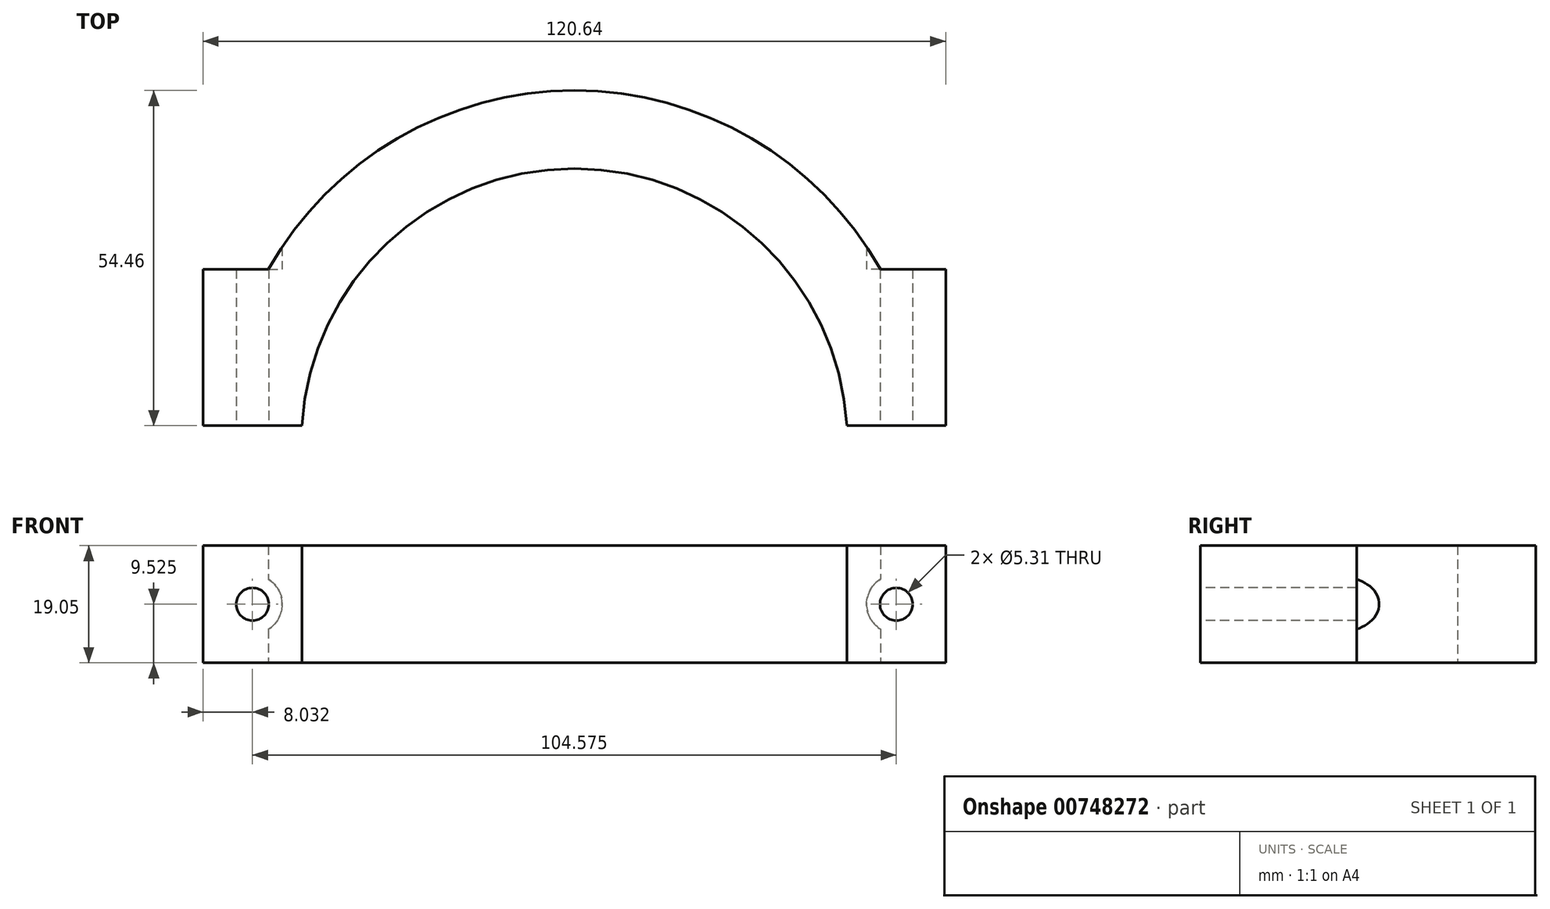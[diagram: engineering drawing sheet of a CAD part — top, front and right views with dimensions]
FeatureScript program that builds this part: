
annotation { "Feature Type Name" : "Feature", "Feature Type Description" : "" }
export const myFeature = defineFeature(function(context is Context, id is Id, definition is map)
    precondition{}
    {
        {
            var Q0;
            Q0=qCreatedBy(makeId("Top.planeOp"),FACE);
            var sketch = newSketch(context, id + "F0", { "sketchPlane" : qUnion([Q0])});
            skPoint(sketch, "E0.middle", {"position": v(0, 24.5) * mm});
            skArc(sketch, "E1", {"start": v(44.25, 27.05) * mm, "mid": v(0, 68.81) * mm, "end": v(-44.25, 27.05) * mm});
            skLineSegment(sketch, "E2", {"start": v(44.25, 27.05) * mm, "end": v(60.33, 27.05) * mm});
            skLineSegment(sketch, "E3", {"start": v(60.33, 27.05) * mm, "end": v(60.33, 52.45) * mm});
            skLineSegment(sketch, "E4", {"start": v(-60.33, 27.05) * mm, "end": v(-60.32, 52.45) * mm});
            skArc(sketch, "E5.0", {"start": v(49.7, 52.45) * mm, "mid": v(0, 81.51) * mm, "end": v(-49.7, 52.45) * mm});
            skLineSegment(sketch, "E6", {"start": v(-60.32, 52.45) * mm, "end": v(-49.7, 52.45) * mm});
            skLineSegment(sketch, "E7", {"start": v(60.33, 52.45) * mm, "end": v(49.7, 52.45) * mm});
            skLineSegment(sketch, "E8", {"start": v(-60.33, 27.05) * mm, "end": v(-44.25, 27.05) * mm});
            skSolve(sketch);
        }
        {
            var Q0;
            Q0 = qSketchRegion(id + "F0", true);
            extrude(context, id + "F1", {"entities" : qUnion([Q0]), "depth" : 19.05 * mm, "offsetDistance" : 25.4 * mm});
        }
        {
            var Q0;
            Q0=makeQuery(id+"F1.opExtrude","SWEPT_FACE",FACE,{"disambiguationData":[OSD([sQuery(id+"F0.wireOp",EDGE,"E8")])]});
            var sketch = newSketch(context, id + "F2", { "sketchPlane" : qUnion([Q0])});
            skLineSegment(sketch, "E9", {"start": v(-52.29, 19.05) * mm, "end": v(-52.29, 0) * mm, "construction": true});
            skLineSegment(sketch, "E10.0", {"start": v(-52.29, 9.53) * mm, "end": v(52.29, 9.53) * mm, "construction": true});
            skCircle(sketch, "E11", {"center": v(-52.29, 9.53) * mm, "radius": 2.65 * mm});
            skCircle(sketch, "E12", {"center": v(52.29, 9.53) * mm, "radius": 2.65 * mm});
            skSolve(sketch);
        }
        {
            var Q0;
            Q0 = qSketchRegion(id + "F2", true);
            extrude(context, id + "F3", {"entities" : qUnion([Q0]), "operationType" : NewBodyOperationType.REMOVE, "endBound" : BoundingType.THROUGH_ALL, "oppositeDirection" : true, "depth" : 25.4 * mm, "offsetDistance" : 25.4 * mm});
        }
        {
            var Q0;
            Q0=makeQuery(id+"F1.opExtrude","SWEPT_FACE",FACE,{"disambiguationData":[OSD([sQuery(id+"F0.wireOp",EDGE,"E7")])]});
            var sketch = newSketch(context, id + "F4", { "sketchPlane" : qUnion([Q0])});
            skLineSegment(sketch, "E13", {"start": v(-52.29, 9.53) * mm, "end": v(52.29, 9.53) * mm, "construction": true});
            skCircle(sketch, "E14", {"center": v(-52.29, 9.53) * mm, "radius": 4.83 * mm});
            skCircle(sketch, "E15", {"center": v(52.29, 9.53) * mm, "radius": 4.83 * mm});
            skLineSegment(sketch, "E16.0", {"start": v(-52.29, 79.38) * mm, "end": v(52.29, 79.38) * mm, "construction": true});
            skCircle(sketch, "E17", {"center": v(-52.29, 79.38) * mm, "radius": 4.83 * mm});
            skCircle(sketch, "E18", {"center": v(52.29, 79.38) * mm, "radius": 4.83 * mm});
            skSolve(sketch);
        }
        {
            var Q0;
            Q0 = qSketchRegion(id + "F4", true);
            extrude(context, id + "F5", {"entities" : qUnion([Q0]), "operationType" : NewBodyOperationType.REMOVE, "depth" : 39.88 * mm, "offsetDistance" : 25.4 * mm});
        }
    });
